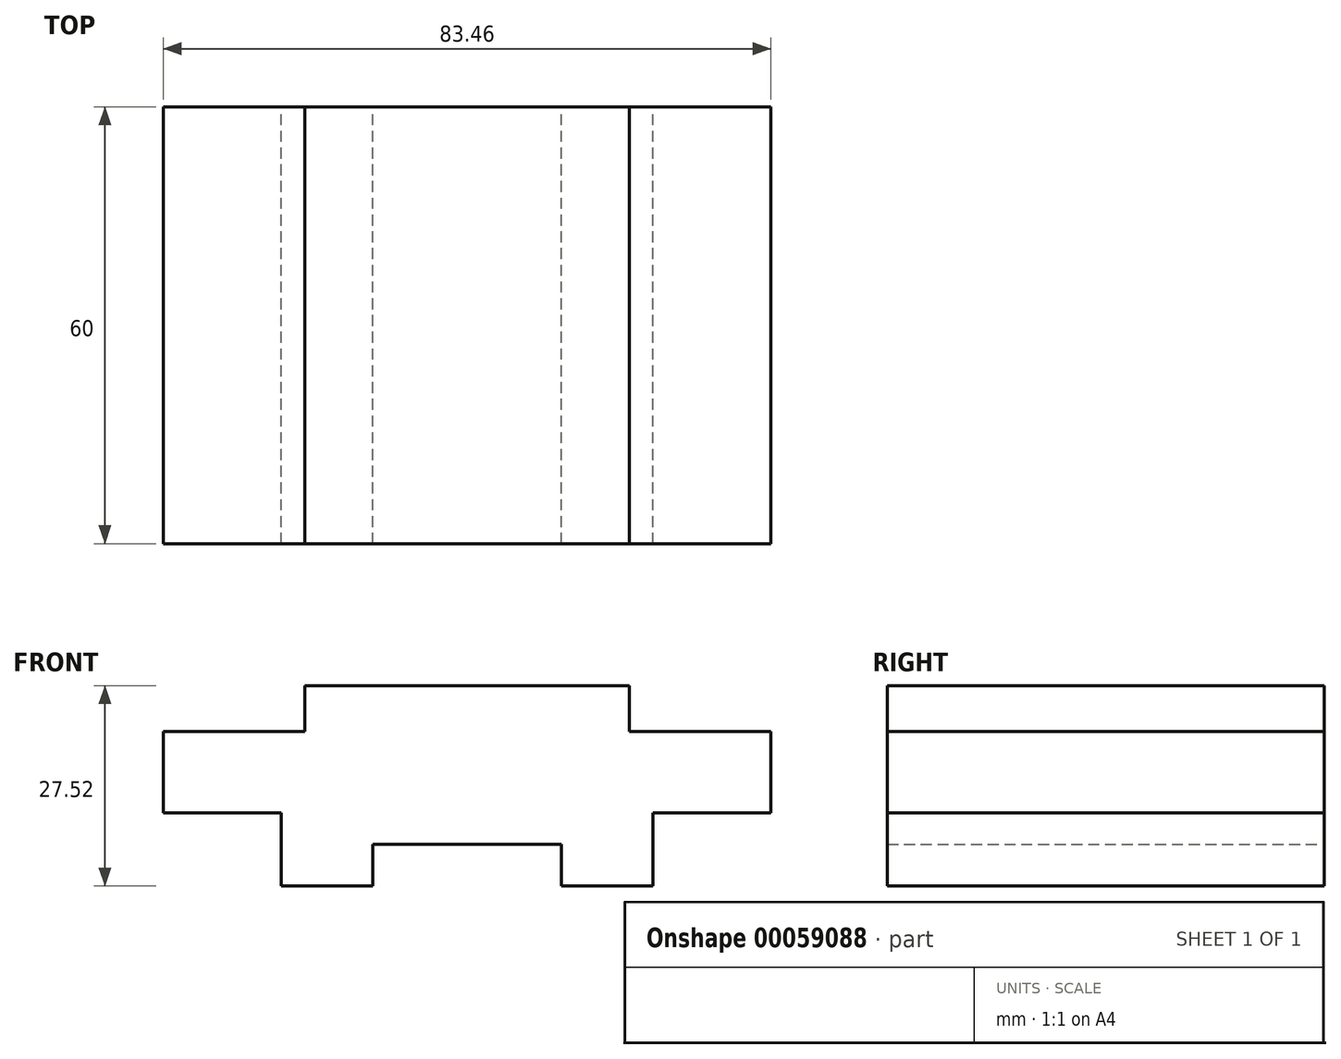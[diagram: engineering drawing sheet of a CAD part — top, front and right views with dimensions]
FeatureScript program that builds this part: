
annotation { "Feature Type Name" : "Feature", "Feature Type Description" : "" }
export const myFeature = defineFeature(function(context is Context, id is Id, definition is map)
    precondition{}
    {
        {
            var Q0;
            Q0=qCreatedBy(makeId("Front.planeOp"),FACE);
            var sketch = newSketch(context, id + "F0", { "sketchPlane" : qUnion([Q0])});
            skLineSegment(sketch, "E0", {"start": v(0, 0) * mm, "end": v(-22.3, 0) * mm});
            skLineSegment(sketch, "E1", {"start": v(-22.3, 0) * mm, "end": v(-22.3, -6.3) * mm});
            skLineSegment(sketch, "E2", {"start": v(-22.3, -6.3) * mm, "end": v(-41.73, -6.3) * mm});
            skLineSegment(sketch, "E3", {"start": v(-41.73, -6.3) * mm, "end": v(-41.73, -17.45) * mm});
            skLineSegment(sketch, "E4", {"start": v(-41.73, -17.45) * mm, "end": v(-25.54, -17.45) * mm});
            skLineSegment(sketch, "E5", {"start": v(-25.54, -17.45) * mm, "end": v(-25.54, -27.52) * mm});
            skLineSegment(sketch, "E6", {"start": v(-25.54, -27.52) * mm, "end": v(-12.95, -27.52) * mm});
            skLineSegment(sketch, "E7", {"start": v(-12.95, -27.52) * mm, "end": v(-12.95, -21.77) * mm});
            skLineSegment(sketch, "E8", {"start": v(-12.95, -21.77) * mm, "end": v(0, -21.77) * mm});
            skLineSegment(sketch, "E9", {"start": v(0, 0) * mm, "end": v(0, 25.72) * mm, "construction": true});
            skLineSegment(sketch, "E10.MirrorCS", {"start": v(22.3, 0) * mm, "end": v(22.3, -6.3) * mm});
            skLineSegment(sketch, "E11.MirrorCS", {"start": v(12.95, -27.52) * mm, "end": v(12.95, -21.77) * mm});
            skLineSegment(sketch, "E12.MirrorCS", {"start": v(25.54, -27.52) * mm, "end": v(12.95, -27.52) * mm});
            skLineSegment(sketch, "E13.MirrorCS", {"start": v(22.3, -6.3) * mm, "end": v(41.73, -6.3) * mm});
            skLineSegment(sketch, "E14.MirrorCS", {"start": v(41.73, -6.3) * mm, "end": v(41.73, -17.45) * mm});
            skLineSegment(sketch, "E15.MirrorCS", {"start": v(41.73, -17.45) * mm, "end": v(25.54, -17.45) * mm});
            skLineSegment(sketch, "E16.MirrorCS", {"start": v(25.54, -17.45) * mm, "end": v(25.54, -27.52) * mm});
            skLineSegment(sketch, "E17.MirrorCS", {"start": v(12.95, -21.77) * mm, "end": v(0, -21.77) * mm});
            skLineSegment(sketch, "E18.MirrorCS", {"start": v(0, 0) * mm, "end": v(22.3, 0) * mm});
            skSolve(sketch);
        }
        {
            var Q0;
            Q0=makeQuery(id+"F0.imprint","IMPRINT",FACE,{"disambiguationData":[TD([[makeQuery(id+"F0.imprint","IMPRINT",EDGE,{"derivedFrom":sQuery(id+"F0.wireOp",EDGE,"E0")}),1.0]])]});
            extrude(context, id + "F1", {"entities" : qUnion([Q0]), "endBound" : BoundingType.SYMMETRIC, "depth" : 60 * mm});
        }
    });
